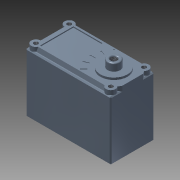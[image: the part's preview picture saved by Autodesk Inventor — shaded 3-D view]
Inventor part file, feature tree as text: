
AUTODESK INVENTOR PART (.ipt)
format: ipt  version: 2013 (Build 170138000, 138)  size: 360,960 bytes
history: native  units: mm
features: sketch x15, extrude x10, hole x5, thread x5, chamfer x4, pattern_circular x2, other x1, fillet x1
ambient origin geometry x1: Origin
feature tree (43):
  other  "ソリッド1"
  extrude  "押し出し1"  Depth=21.0mm
  hole  "穴1"  [1 undecoded]
  extrude  "押し出し2"  Depth=41.0mm
  extrude  "押し出し3"  Depth=20.5mm
  hole  "穴2"  [1 undecoded]
  extrude  "押し出し4"  Depth=2.0mm
  pattern_circular  "円形状パターン1"  [2 undecoded]
  extrude  "押し出し5"  Depth=36.0mm
  chamfer  "面取り1"  Distance=16.0mm
  chamfer  "面取り2"  Distance=16.0mm
  chamfer  "面取り3"  Distance=2.5mm
  extrude  "押し出し6"  Depth=2.5mm
  hole  "穴3"  [1 undecoded]
  extrude  "押し出し7"  Depth=2.5mm
  extrude  "押し出し8"  Depth=13.0mm
  hole  "穴4"  [1 undecoded]
  extrude  "押し出し9"  Depth=10.5mm
  pattern_circular  "円形状パターン2"  [2 undecoded]
  extrude  "押し出し10"  Depth=6.0mm
  chamfer  "面取り5"  Distance=3.5mm
  fillet  "フィレット2"  Radius=3.0mm
  thread  "ねじ1"
  thread  "ねじ2"
  thread  "ねじ3"
  thread  "ねじ4"
  thread  "ねじ5"
  hole  "穴5"  [1 undecoded]
  sketch  "スケッチ1"
  sketch  "スケッチ2"
  sketch  "スケッチ3"
  sketch  "スケッチ4"
  sketch  "スケッチ5"
  sketch  "スケッチ6"
  sketch  "スケッチ8"
  sketch  "スケッチ10"
  sketch  "スケッチ12"
  sketch  "スケッチ13"
  sketch  "スケッチ14"
  sketch  "スケッチ15"
  sketch  "スケッチ16"
  sketch  "スケッチ18"
  sketch  "スケッチ19"
note: 9 required parameter values undecoded (feature->parameter linkage not recoverable at this tier; creation-order binding heuristic only, values carry confidence <= 0.55)
